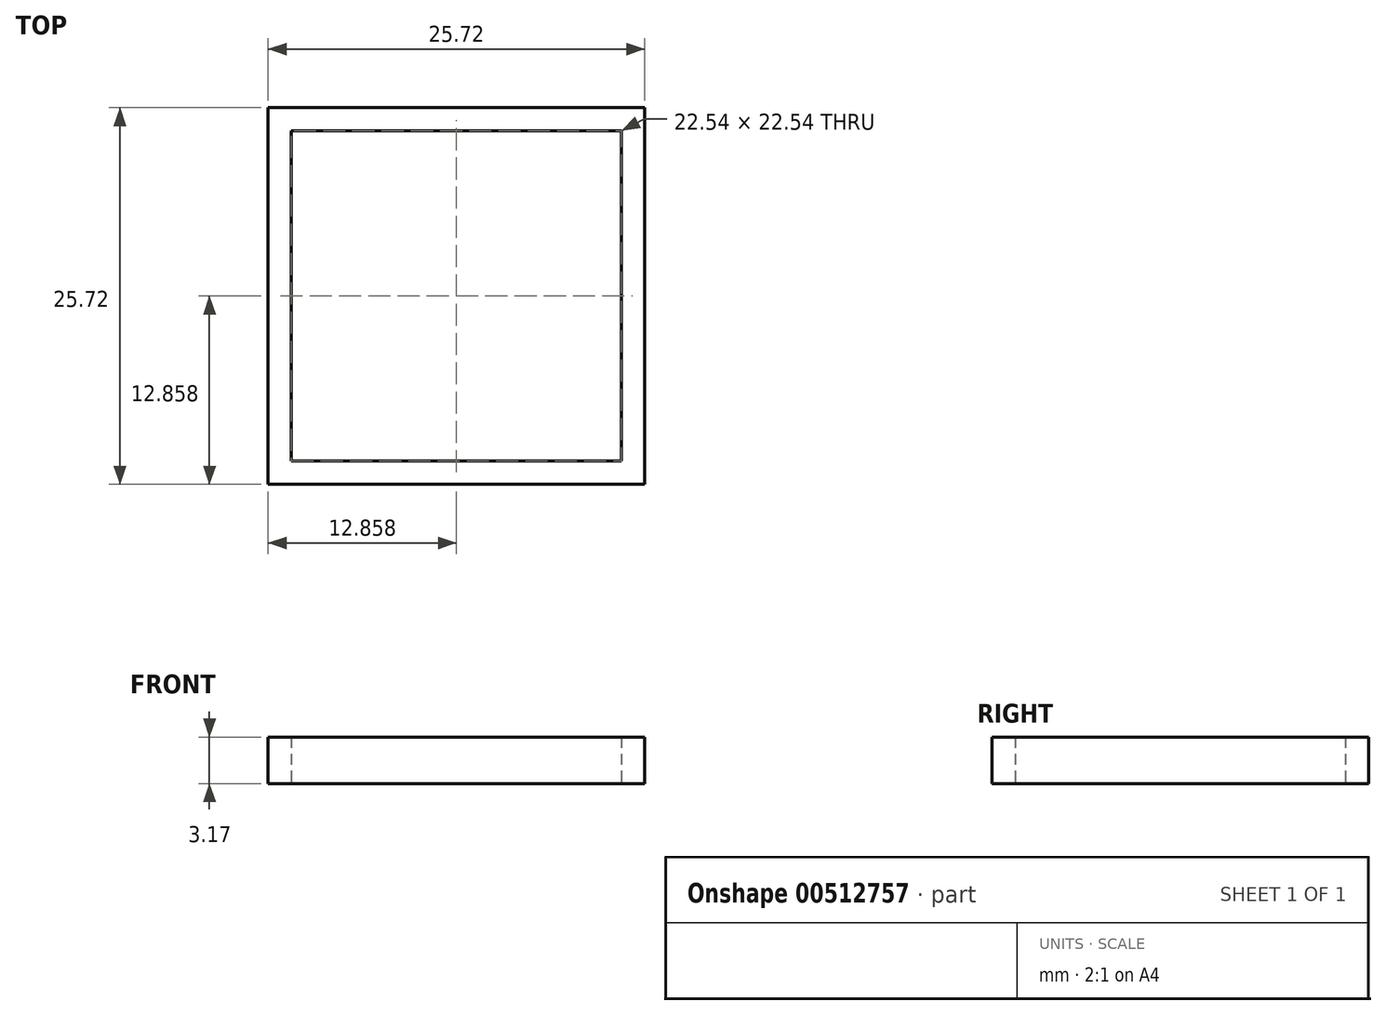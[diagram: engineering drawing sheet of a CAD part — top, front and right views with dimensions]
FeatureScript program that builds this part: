
annotation { "Feature Type Name" : "Feature", "Feature Type Description" : "" }
export const myFeature = defineFeature(function(context is Context, id is Id, definition is map)
    precondition{}
    {
        {
            var Q0;
            Q0=qCreatedBy(makeId("Top.planeOp"),FACE);
            var sketch = newSketch(context, id + "F0", { "sketchPlane" : qUnion([Q0])});
            skLineSegment(sketch, "E0", {"start": v(0, 0) * mm, "end": v(0, 25.72) * mm});
            skLineSegment(sketch, "E1", {"start": v(0, 25.72) * mm, "end": v(25.72, 25.72) * mm});
            skLineSegment(sketch, "E2.bottom", {"start": v(0, 0) * mm, "end": v(25.72, 0) * mm});
            skLineSegment(sketch, "E2.right", {"start": v(25.72, 0) * mm, "end": v(25.72, 25.72) * mm});
            skLineSegment(sketch, "E3", {"start": v(1.59, 24.13) * mm, "end": v(24.13, 24.13) * mm});
            skLineSegment(sketch, "E4", {"start": v(1.59, 24.13) * mm, "end": v(1.59, 1.59) * mm});
            skLineSegment(sketch, "E5", {"start": v(24.13, 24.13) * mm, "end": v(24.13, 1.59) * mm});
            skLineSegment(sketch, "E6", {"start": v(24.13, 1.59) * mm, "end": v(1.59, 1.59) * mm});
            skPoint(sketch, "E7.orphan", {"position": v(12.86, 12.86) * mm});
            skSolve(sketch);
        }
        {
            var Q0;
            Q0 = qSketchRegion(id + "F0", true);
            extrude(context, id + "F1", {"entities" : qUnion([Q0]), "depth" : 3.17 * mm});
        }
    });
